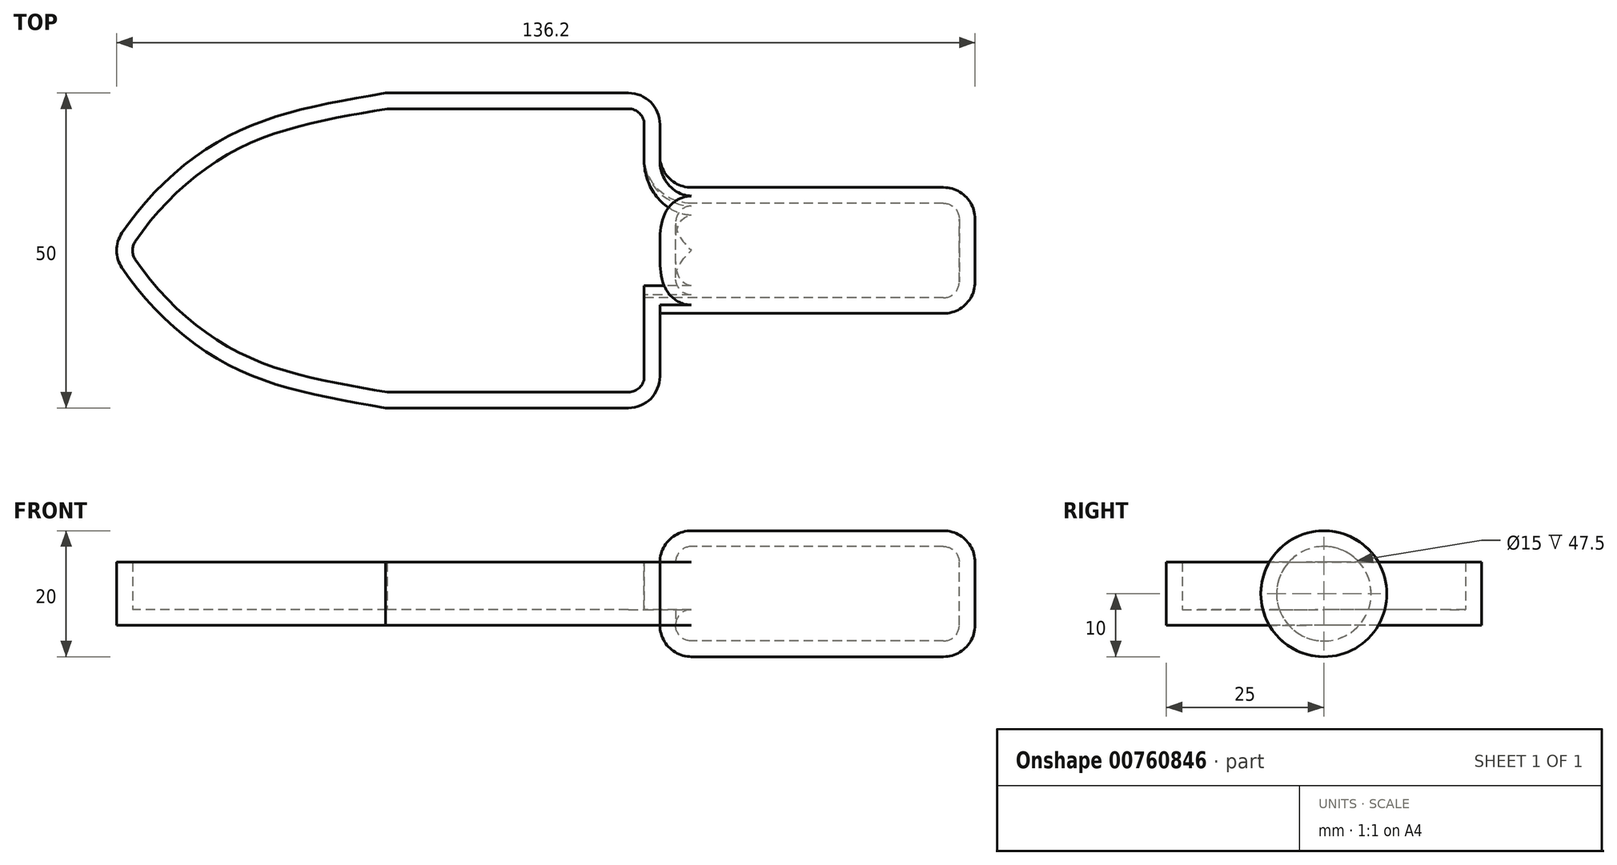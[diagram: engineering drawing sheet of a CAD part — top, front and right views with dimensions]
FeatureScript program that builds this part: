
annotation { "Feature Type Name" : "Feature", "Feature Type Description" : "" }
export const myFeature = defineFeature(function(context is Context, id is Id, definition is map)
    precondition{}
    {
        {
            var Q0;
            Q0=qCreatedBy(makeId("Top.planeOp"),FACE);
            var sketch = newSketch(context, id + "F0", { "sketchPlane" : qUnion([Q0])});
            skLineSegment(sketch, "E0.bottom", {"start": v(43.52, 25) * mm, "end": v(-43.52, 25) * mm});
            skLineSegment(sketch, "E0.top", {"start": v(43.52, -25) * mm, "end": v(-43.52, -25) * mm});
            skLineSegment(sketch, "E0.left", {"start": v(43.52, 25) * mm, "end": v(43.52, -25) * mm});
            skLineSegment(sketch, "E0.right", {"start": v(-43.52, 25) * mm, "end": v(-43.52, -25) * mm});
            skPoint(sketch, "E0.middle", {"position": v(0, 0) * mm});
            skFitSpline(sketch, "E1", {"points": [v(0, 25) * mm, v(-25.98, 17.6) * mm, v(-43.52, 0) * mm], "startDerivative": vector(-59.3, -10.25) * mm, "endDerivative": vector(-23.28, -42.12) * mm});
            skLineSegment(sketch, "E2", {"start": v(-43.52, 0) * mm, "end": v(43.52, 0) * mm});
            skFitSpline(sketch, "E3.MirrorCS", {"points": [v(0, -25) * mm, v(-25.98, -17.6) * mm, v(-43.52, 0) * mm], "startDerivative": vector(-59.3, 10.25) * mm, "endDerivative": vector(-23.28, 42.12) * mm});
            skSolve(sketch);
        }
        {
            var Q0;
            {var subQ4=sQuery(id+"F0.wireOp",EDGE,"E2");Q0=makeQuery(id+"F0.imprint","IMPRINT",FACE,{"disambiguationData":[TD([[makeQuery(id+"F0.imprint","IMPRINT",EDGE,{"derivedFrom":subQ4}),-1.0]])]});}
            var Q1;
            {var subQ3=sQuery(id+"F0.wireOp",EDGE,"E1");Q1=makeQuery(id+"F0.imprint","IMPRINT",FACE,{"disambiguationData":[TD([[makeQuery(id+"F0.imprint","IMPRINT",EDGE,{"derivedFrom":subQ3}),1.0]])]});}
            extrude(context, id + "F1", {"entities" : qUnion([Q0, Q1]), "endBound" : BoundingType.SYMMETRIC, "depth" : 10 * mm, "offsetDistance" : 25 * mm});
        }
        {
            var Q0;
            Q0=makeQuery(id+"F1.opExtrude","SWEPT_FACE",FACE,{"disambiguationData":[OSD([sQuery(id+"F0.wireOp",EDGE,"E0.left")])]});
            var sketch = newSketch(context, id + "F2", { "sketchPlane" : qUnion([Q0])});
            skCircle(sketch, "E4", {"center": v(0, 0) * mm, "radius": 10 * mm});
            skSolve(sketch);
        }
        {
            var Q0;
            Q0 = qSketchRegion(id + "F2", true);
            extrude(context, id + "F3", {"entities" : qUnion([Q0]), "operationType" : NewBodyOperationType.ADD, "depth" : 50 * mm, "offsetDistance" : 25 * mm});
        }
        {
            var Q0;
            Q0=makeQuery(id+"F1.opExtrude","SWEPT_EDGE",EDGE,{"disambiguationData":[OSD([sQuery(id+"F0.wireOp",EDGE,"E0.right"),sQuery(id+"F0.wireOp",EDGE,"E1"),sQuery(id+"F0.wireOp",EDGE,"E2"),sQuery(id+"F0.wireOp",EDGE,"E3.MirrorCS")])]});
            var Q1;
            Q1=makeQuery(id+"F1.opExtrude","SWEPT_EDGE",EDGE,{"disambiguationData":[OSD([sQuery(id+"F0.wireOp",EDGE,"E0.top"),sQuery(id+"F0.wireOp",EDGE,"E0.left")])]});
            var Q2;
            Q2=makeQuery(id+"F1.opExtrude","SWEPT_EDGE",EDGE,{"disambiguationData":[OSD([sQuery(id+"F0.wireOp",EDGE,"E0.bottom"),sQuery(id+"F0.wireOp",EDGE,"E0.left")])]});
            fillet(context, id + "F4", {"entities" : qUnion([Q0, Q1, Q2]), "radius" : 5 * mm, "tangentPropagation" : true, "allowEdgeOverflow" : false});
        }
        {
            var Q0;
            {var subQ0=sQuery(id+"F0.wireOp",EDGE,"E0.left");var subQ1=sQuery(id+"F2.wireOp",EDGE,"E4");var subQ2=makeQuery(id+"F3.opExtrude","CAP_FACE",FACE,{"disambiguationData":[OSD([subQ1])],"isStart":true});var subQ3=makeQuery(id+"F3.opExtrude","SWEPT_FACE",FACE,{"disambiguationData":[OSD([subQ1])]});Q0=makeQuery(id+"F3.boolean.opBoolean","SPLIT",EDGE,{"disambiguationData":[topologyDisambiguationEdgeConnected([subQ3,subQ2]),TD([makeQuery(id+"F1.opExtrude","CAP_FACE",FACE,{"disambiguationData":[OSD([sQuery(id+"F0.wireOp",EDGE,"E0.bottom"),sQuery(id+"F0.wireOp",EDGE,"E0.top"),subQ0,sQuery(id+"F0.wireOp",EDGE,"E1"),sQuery(id+"F0.wireOp",EDGE,"E3.MirrorCS")])],"isStart":true})])],"derivedFrom":makeQuery(id+"F3.opExtrude","CAP_EDGE",EDGE,{"disambiguationData":[OSD([subQ1])],"isStart":true})});}
            var Q1;
            {var subQ0=sQuery(id+"F0.wireOp",EDGE,"E0.left");var subQ1=sQuery(id+"F2.wireOp",EDGE,"E4");var subQ2=makeQuery(id+"F3.opExtrude","CAP_FACE",FACE,{"disambiguationData":[OSD([subQ1])],"isStart":true});var subQ3=makeQuery(id+"F3.opExtrude","SWEPT_FACE",FACE,{"disambiguationData":[OSD([subQ1])]});Q1=makeQuery(id+"F3.boolean.opBoolean","SPLIT",EDGE,{"disambiguationData":[topologyDisambiguationEdgeConnected([subQ3,subQ2]),TD([makeQuery(id+"F1.opExtrude","CAP_FACE",FACE,{"disambiguationData":[OSD([sQuery(id+"F0.wireOp",EDGE,"E0.bottom"),sQuery(id+"F0.wireOp",EDGE,"E0.top"),subQ0,sQuery(id+"F0.wireOp",EDGE,"E1"),sQuery(id+"F0.wireOp",EDGE,"E3.MirrorCS")])],"isStart":false})])],"derivedFrom":makeQuery(id+"F3.opExtrude","CAP_EDGE",EDGE,{"disambiguationData":[OSD([subQ1])],"isStart":true})});}
            var Q2;
            Q2=makeQuery(id+"F3.opExtrude","CAP_EDGE",EDGE,{"disambiguationData":[OSD([sQuery(id+"F2.wireOp",EDGE,"E4")])],"isStart":false});
            fillet(context, id + "F5", {"entities" : qUnion([Q0, Q1, Q2]), "radius" : 5 * mm, "tangentPropagation" : true, "allowEdgeOverflow" : false});
        }
        {
            var Q0;
            {var subQ0=sQuery(id+"F2.wireOp",EDGE,"E4");Q0=makeQuery(id+"F3.boolean.opBoolean","SPLIT",EDGE,{"disambiguationData":[topologyDisambiguationEdgeConnected([makeQuery(id+"F1.opExtrude","SWEPT_FACE",FACE,{"disambiguationData":[OSD([sQuery(id+"F0.wireOp",EDGE,"E0.left")])]}),makeQuery(id+"F3.opExtrude","SWEPT_FACE",FACE,{"disambiguationData":[OSD([subQ0])]})]),OD(0.0)],"derivedFrom":makeQuery(id+"F3.opExtrude","CAP_EDGE",EDGE,{"disambiguationData":[OSD([subQ0])],"isStart":true})});}
            var Q1;
            {var subQ0=sQuery(id+"F2.wireOp",EDGE,"E4");Q1=makeQuery(id+"F3.boolean.opBoolean","SPLIT",EDGE,{"disambiguationData":[topologyDisambiguationEdgeConnected([makeQuery(id+"F1.opExtrude","SWEPT_FACE",FACE,{"disambiguationData":[OSD([sQuery(id+"F0.wireOp",EDGE,"E0.left")])]}),makeQuery(id+"F3.opExtrude","SWEPT_FACE",FACE,{"disambiguationData":[OSD([subQ0])]})]),OD(1.0)],"derivedFrom":makeQuery(id+"F3.opExtrude","CAP_EDGE",EDGE,{"disambiguationData":[OSD([subQ0])],"isStart":true})});}
            fillet(context, id + "F6", {"entities" : qUnion([Q0, Q1]), "radius" : 5 * mm, "tangentPropagation" : true, "allowEdgeOverflow" : false});
        }
        {
            var Q0;
            Q0=makeQuery(id+"F1.opExtrude","CAP_FACE",FACE,{"disambiguationData":[OSD([sQuery(id+"F0.wireOp",EDGE,"E0.bottom"),sQuery(id+"F0.wireOp",EDGE,"E0.top"),sQuery(id+"F0.wireOp",EDGE,"E0.left"),sQuery(id+"F0.wireOp",EDGE,"E1"),sQuery(id+"F0.wireOp",EDGE,"E3.MirrorCS")])],"isStart":false});
            shell(context, id + "F7", {"entities" : qUnion([Q0]), "thickness" : 2.5 * mm});
        }
    });
